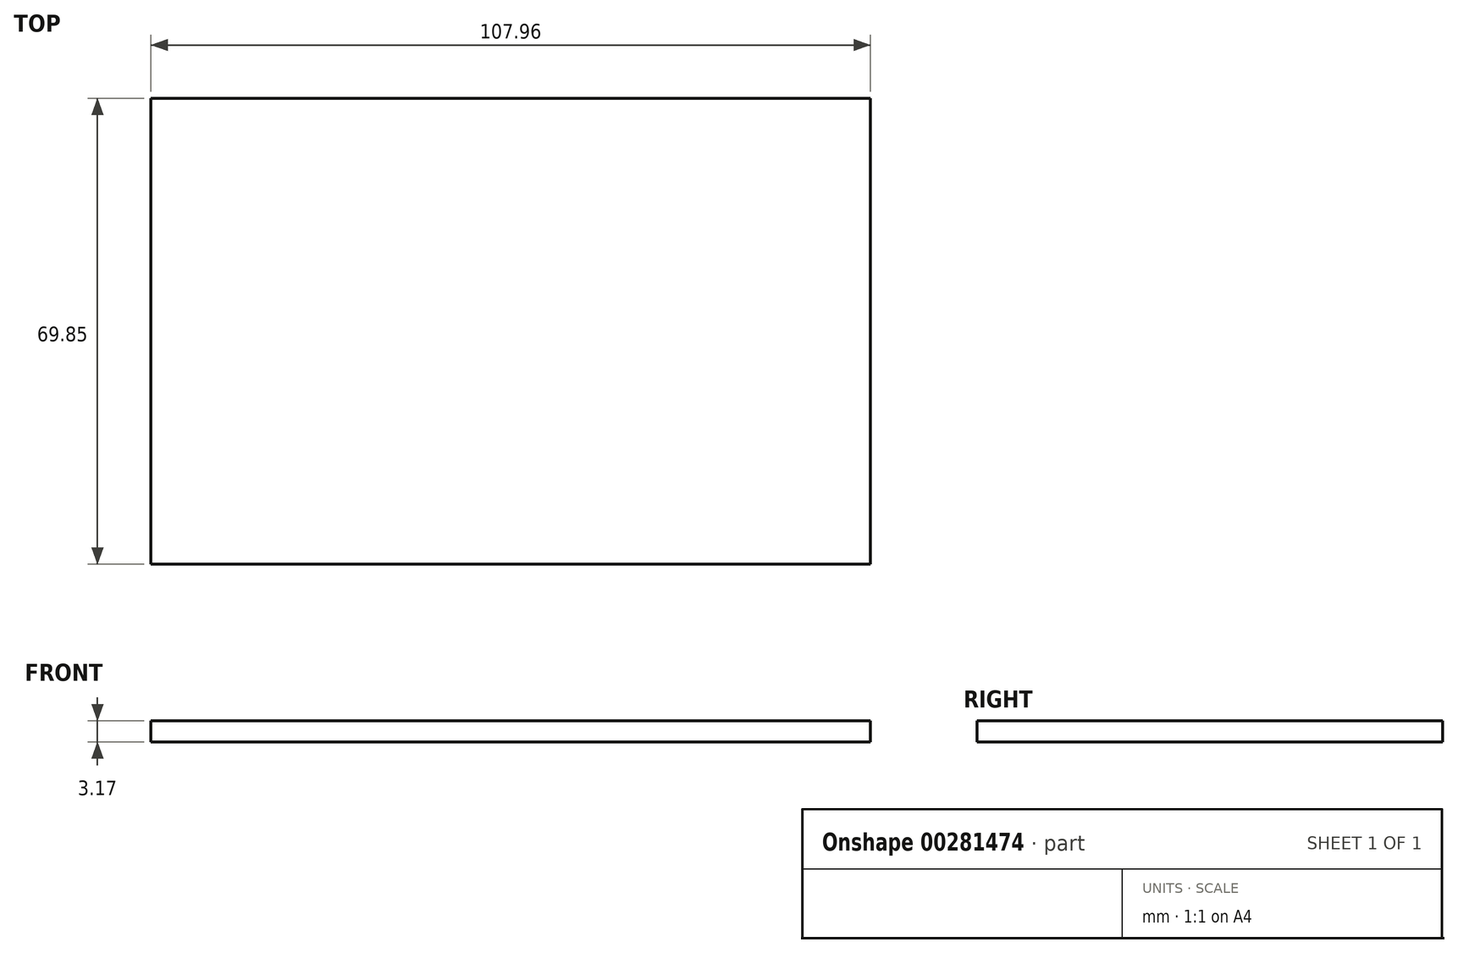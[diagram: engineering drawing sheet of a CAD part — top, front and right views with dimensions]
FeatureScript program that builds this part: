
annotation { "Feature Type Name" : "Feature", "Feature Type Description" : "" }
export const myFeature = defineFeature(function(context is Context, id is Id, definition is map)
    precondition{}
    {
        {
            var Q0;
            Q0=qCreatedBy(makeId("Top.planeOp"),FACE);
            var sketch = newSketch(context, id + "F0", { "sketchPlane" : qUnion([Q0])});
            skLineSegment(sketch, "E0.bottom", {"start": v(53.97, 37.21) * mm, "end": v(-53.98, 37.21) * mm});
            skLineSegment(sketch, "E0.top", {"start": v(53.98, -32.64) * mm, "end": v(-53.97, -32.64) * mm});
            skLineSegment(sketch, "E0.left", {"start": v(53.97, 37.21) * mm, "end": v(53.98, -32.64) * mm});
            skLineSegment(sketch, "E0.right", {"start": v(-53.98, 37.21) * mm, "end": v(-53.98, -32.64) * mm});
            skPoint(sketch, "E0.middle", {"position": v(0, 2.29) * mm});
            skSolve(sketch);
        }
        {
            var Q0;
            Q0 = qSketchRegion(id + "F0", true);
            var Q1;
            Q1 = qConstructionFilter(qBodyType(qCreatedBy(id + "F0" ,EDGE), BodyType.WIRE), ConstructionObject.NO);
            extrude(context, id + "F1", {"entities" : qUnion([Q0]), "surfaceEntities" : qUnion([Q1]), "oppositeDirection" : true, "depth" : 3.17 * mm});
        }
    });
